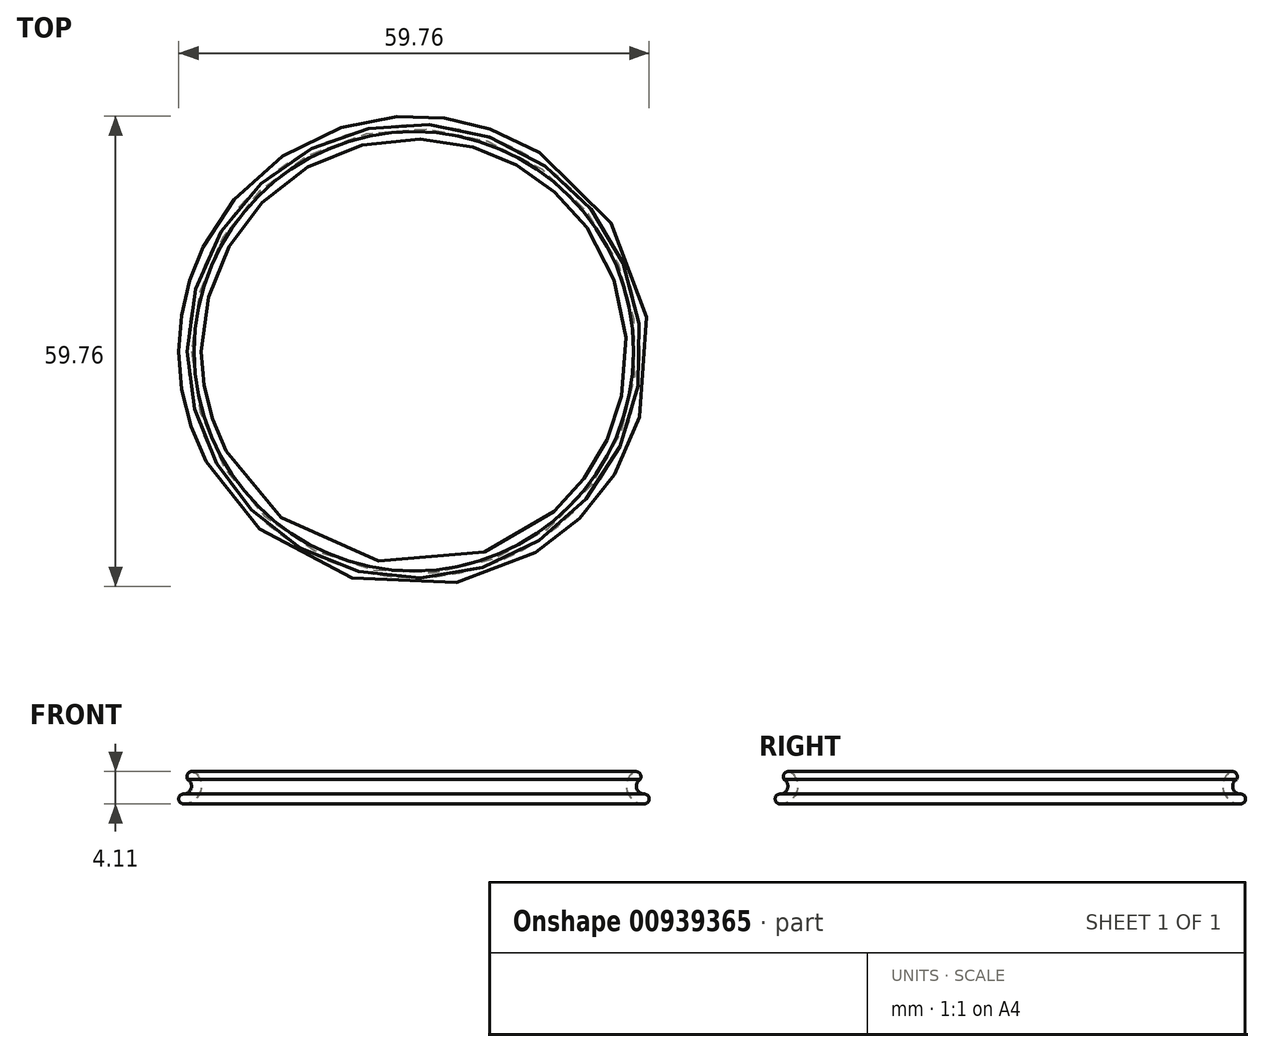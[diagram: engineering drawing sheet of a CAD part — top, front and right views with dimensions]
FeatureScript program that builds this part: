
annotation { "Feature Type Name" : "Feature", "Feature Type Description" : "" }
export const myFeature = defineFeature(function(context is Context, id is Id, definition is map)
    precondition{}
    {
        {
            var Q0;
            Q0=qCreatedBy(makeId("Top.planeOp"),FACE);
            var sketch = newSketch(context, id + "F0", { "sketchPlane" : qUnion([Q0])});
            skCircle(sketch, "E0", {"center": v(0, 0) * mm, "radius": 29.25 * mm});
            skSolve(sketch);
        }
        {
            var Q0;
            Q0=qCreatedBy(makeId("Front.planeOp"),FACE);
            var sketch = newSketch(context, id + "F1", { "sketchPlane" : qUnion([Q0])});
            skCircle(sketch, "E1", {"center": v(-29.25, 0) * mm, "radius": 1 * mm});
            skCircle(sketch, "E2", {"center": v(-29.25, 0) * mm, "radius": 2.25 * mm});
            skLineSegment(sketch, "E3", {"start": v(-28.25, 0) * mm, "end": v(-29.25, 0) * mm});
            skLineSegment(sketch, "E4", {"start": v(-28.25, 0) * mm, "end": v(-28.75, 0.87) * mm});
            skLineSegment(sketch, "E5", {"start": v(-28.75, 0.87) * mm, "end": v(-27.6, 1.53) * mm});
            skCircle(sketch, "E6", {"center": v(-28.18, 1.2) * mm, "radius": 0.66 * mm});
            skLineSegment(sketch, "E7", {"start": v(-29.25, -2.25) * mm, "end": v(-29.25, -1) * mm});
            skCircle(sketch, "E8", {"center": v(-29.25, -1.63) * mm, "radius": 0.63 * mm});
            skLineSegment(sketch, "E9", {"start": v(-27, 0) * mm, "end": v(-27, -2.25) * mm});
            skLineSegment(sketch, "E10", {"start": v(-27, -2.25) * mm, "end": v(-29.25, -2.25) * mm});
            skSolve(sketch);
        }
        {
            var Q0;
            {var subQ1=sQuery(id+"F1.wireOp",EDGE,"E5");Q0=makeQuery(id+"F1.imprint","IMPRINT",FACE,{"disambiguationData":[TD([[makeQuery(id+"F1.imprint","IMPRINT",EDGE,{"derivedFrom":subQ1}),1.0]])]});}
            var Q1;
            {var subQ1=sQuery(id+"F1.wireOp",EDGE,"E5");Q1=makeQuery(id+"F1.imprint","IMPRINT",FACE,{"disambiguationData":[TD([[makeQuery(id+"F1.imprint","IMPRINT",EDGE,{"derivedFrom":subQ1}),-1.0]])]});}
            var Q2;
            {var subQ5=sQuery(id+"F1.wireOp",EDGE,"E1");var subQ10=makeQuery(id+"F1.imprint","INTERSECT",VERTEX,{"derivedFrom":[subQ5,sQuery(id+"F1.wireOp",EDGE,"E4")]});Q2=makeQuery(id+"F1.imprint","IMPRINT",FACE,{"disambiguationData":[TD([[makeQuery(id+"F1.imprint","IMPRINT",EDGE,{"disambiguationData":[TD([[subQ10,-1.0]])],"derivedFrom":subQ5}),-1.0]])]});}
            var Q3;
            {var subQ0=sQuery(id+"F1.wireOp",EDGE,"E7");Q3=makeQuery(id+"F1.imprint","IMPRINT",FACE,{"disambiguationData":[TD([[makeQuery(id+"F1.imprint","IMPRINT",EDGE,{"derivedFrom":subQ0}),-1.0]])]});}
            var Q4;
            {var subQ0=sQuery(id+"F1.wireOp",EDGE,"E7");Q4=makeQuery(id+"F1.imprint","IMPRINT",FACE,{"disambiguationData":[TD([[makeQuery(id+"F1.imprint","IMPRINT",EDGE,{"derivedFrom":subQ0}),1.0]])]});}
            var Q5;
            Q5=sQuery(id+"F0.wireOp",EDGE,"E0");
            sweep(context, id + "F2", {"profiles" : qUnion([Q0, Q1, Q2, Q3, Q4]), "path" : qUnion([Q5])});
        }
    });
